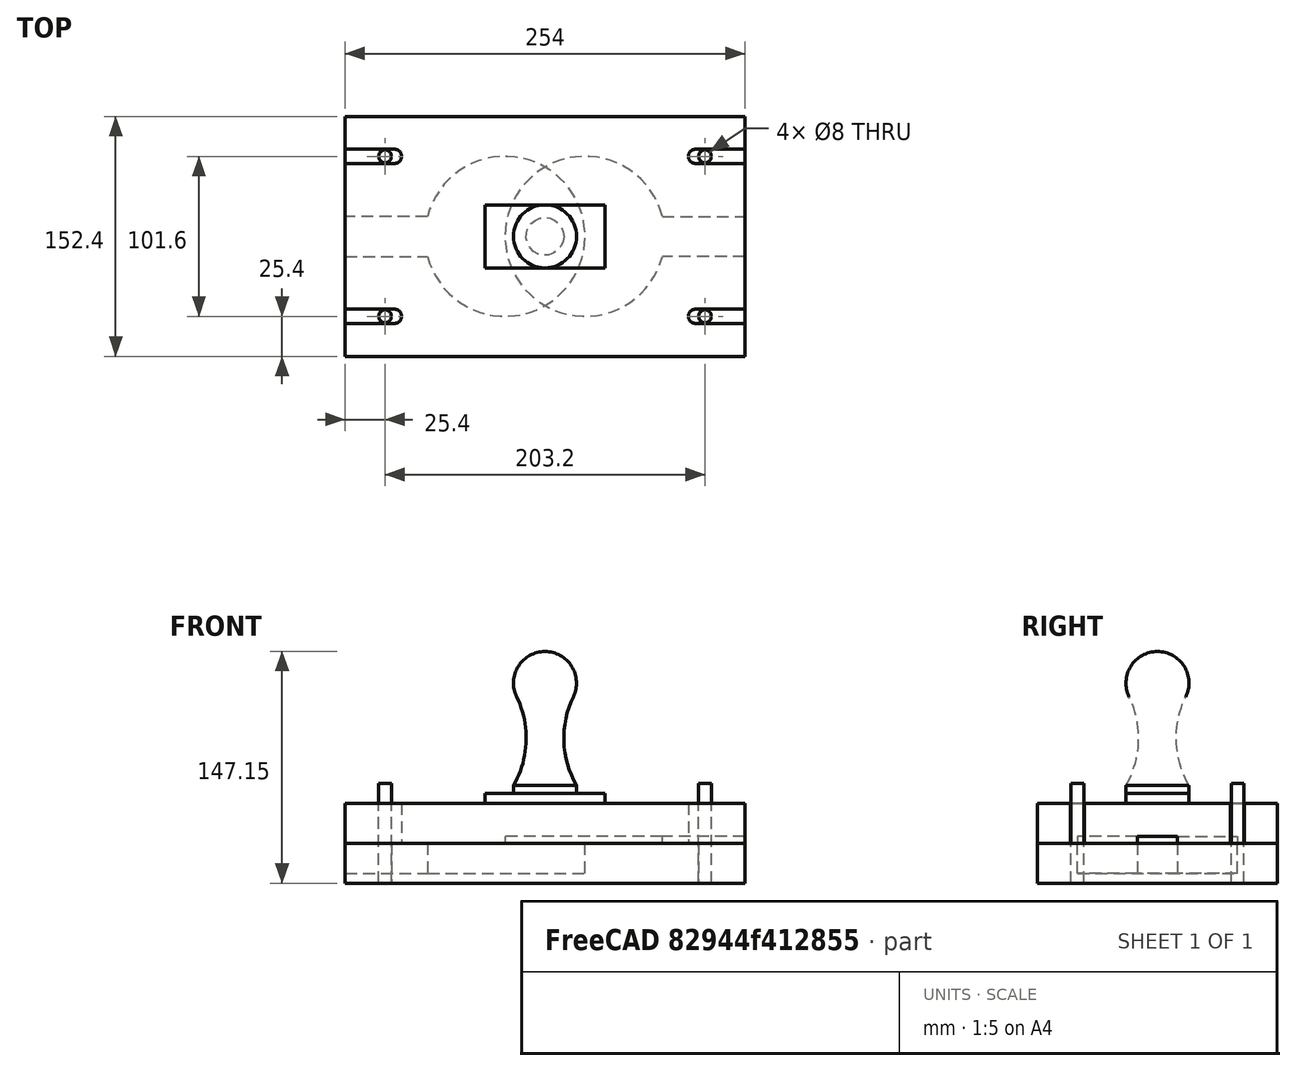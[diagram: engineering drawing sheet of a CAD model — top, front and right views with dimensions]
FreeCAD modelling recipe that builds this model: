
FCSTD DOCUMENT  (FreeCAD 0.17R13541 (Git))
Label: Bell-metal-detector-FEM
License: All rights reserved
LicenseURL: http://en.wikipedia.org/wiki/All_rights_reserved
objects: Sketcher::SketchObject×8, PartDesign::Pocket×4, Part::Cylinder×4, PartDesign::Mirrored×4, PartDesign::Pad×3, PartDesign::Body×3, Fem::FemSolverObjectPython×3, Fem::FemMeshObjectPython×3, PartDesign::MultiTransform×2, PartDesign::ShapeBinder×2, Part::Feature×2, Fem::ConstraintFixed×2, Fem::ConstraintForce×2, App::MaterialObjectPython×2, Fem::FemResultObjectPython×2, Fem::FemAnalysis×2, PartDesign::Revolution×1, Part::Compound×1, Part::Fuse×1, Fem::FemMeshShapeNetgenObject×1
note: 43 computed .brp shape members not serialized (recipe doc carries the construction recipe); baked Part::Feature solids carry a one-line shape summary decoded from their .brp

FEATURE [Sketcher::SketchObject] Sketch
  MapMode = 5
  Support = -> [XY_Plane]
  sketch-geometry (4):
    g0: LineSegment StartX=127 StartY=76.2 StartZ=0 EndX=-127 EndY=76.2 EndZ=0
    g1: LineSegment StartX=-127 StartY=76.2 StartZ=0 EndX=-127 EndY=-76.2 EndZ=0
    g2: LineSegment StartX=-127 StartY=-76.2 StartZ=0 EndX=127 EndY=-76.2 EndZ=0
    g3: LineSegment StartX=127 StartY=-76.2 StartZ=0 EndX=127 EndY=76.2 EndZ=0
  constraints (11):
    c: Coincident(g0,g1)
    c: Coincident(g1,g2)
    c: Coincident(g2,g3)
    c: Coincident(g3,g0)
    c: Horizontal(g0)
    c: Horizontal(g2)
    c: Vertical(g1)
    c: Vertical(g3)
    c: DistanceX(g0,g0) = 254
    c: DistanceY(g2,g0) = 152.4
    c: Symmetric(g0,g1,g-1)
FEATURE [PartDesign::Pad] Pad  label="上基座"
  Length = 25.4
  Length2 = 100
  Profile = -> Sketch
  Type = 0
FEATURE [Sketcher::SketchObject] Sketch001
  MapMode = 5
  Placement = pos=(0,0,25.4) rot=(0,0,1;0rad)
  Support = -> [Pad]
  sketch-geometry (1):
    g0: Circle CenterX=-101.6 CenterY=50.8 CenterZ=0 NormalX=0 NormalY=0 NormalZ=1 AngleXU=0 Radius=4
  constraints (3):
    c: DistanceX(g0) = -101.6
    c: DistanceY(g0) = 50.8
    c: Radius(g0) = 4
FEATURE [PartDesign::Pocket] Pocket  label="销钉孔"
  BaseFeature = -> Pad
  Length = 5
  Length2 = 100
  Profile = -> Sketch001
  Type = 1
FEATURE [Part::Cylinder] Cylinder  label="销钉1"
  Angle = 360
  AttacherType = Attacher::AttachEngine3D
  Height = 63.5
  Placement = pos=(-101.6,50.8,0) rot=(0,0,1;0rad)
  Radius = 4
FEATURE [Part::Cylinder] Cylinder001  label="销钉2"
  Angle = 360
  AttacherType = Attacher::AttachEngine3D
  Height = 63.5
  Placement = pos=(101.6,50.8,0) rot=(0,0,1;0rad)
  Radius = 4
FEATURE [Part::Cylinder] Cylinder002  label="销钉3"
  Angle = 360
  AttacherType = Attacher::AttachEngine3D
  Height = 63.5
  Placement = pos=(-101.6,-50.8,0) rot=(0,0,1;0rad)
  Radius = 4
FEATURE [Part::Cylinder] Cylinder003  label="销钉4"
  Angle = 360
  AttacherType = Attacher::AttachEngine3D
  Height = 63.5
  Placement = pos=(101.6,-50.8,0) rot=(0,0,1;0rad)
  Radius = 4
FEATURE [PartDesign::Mirrored] Mirrored
  MirrorPlane = -> YZ_Plane
FEATURE [PartDesign::Mirrored] Mirrored001
  MirrorPlane = -> XZ_Plane
FEATURE [PartDesign::MultiTransform] MultiTransform  label="两次镜像的销钉孔"
  BaseFeature = -> Pocket
  Originals = -> [Pocket]
  Transformations = -> [Mirrored,Mirrored001]
FEATURE [Sketcher::SketchObject] Sketch002
  ExternalGeometry = -> [MultiTransform]
  MapMode = 5
  Placement = pos=(0,0,25.4) rot=(0,0,1;0rad)
  Support = -> [MultiTransform]
  sketch-geometry (4):
    g0: LineSegment StartX=-127 StartY=-12.7 StartZ=0 EndX=-74.5869 EndY=-12.7 EndZ=0
    g1: LineSegment StartX=-74.5869 StartY=12.7 StartZ=0 EndX=-127 EndY=12.7 EndZ=0
    g2: LineSegment StartX=-127 StartY=12.7 StartZ=0 EndX=-127 EndY=-12.7 EndZ=0
    g3: ArcOfCircle CenterX=-25.4 CenterY=0 CenterZ=0 NormalX=0 NormalY=0 NormalZ=1 AngleXU=0 Radius=50.8 StartAngle=3.39427 EndAngle=9.1721
  constraints (13):
    c: Coincident(g1,g2)
    c: Coincident(g2,g0)
    c: Horizontal(g0)
    c: Horizontal(g1)
    c: Vertical(g2)
    c: PointOnObject(g0,g-3)
    c: PointOnObject(g3,g-1)  '凹坑中心在x轴上'
    c: Symmetric(g1,g0,g-1)  '沟槽中心对称'
    c: DistanceY(g0,g1) = 25.4  '沟槽宽度'
    c: Radius(g3) = 50.8  '凹坑半径'
    c: DistanceX(g3,g-1) = 25.4  '凹坑位置'
    c: Coincident(g3,g0)
    c: Coincident(g3,g1)
FEATURE [PartDesign::Pocket] Pocket001  label="深沟槽和凹坑"
  BaseFeature = -> MultiTransform
  Length = 19.05
  Length2 = 100
  Profile = -> Sketch002
  Type = 0
FEATURE [PartDesign::Body] Body  label="下底座"
  Group = -> [Sketch,Pad,Sketch001,Pocket,MultiTransform,Mirrored,Mirrored001,Sketch002,Pocket001]
  Origin = -> Origin
  Tip = -> Pocket001
FEATURE [PartDesign::ShapeBinder] ShapeBinder  label="引用的下底座的顶面"
  Support = -> [Pocket001]
FEATURE [Sketcher::SketchObject] Sketch003
  ExternalGeometry = -> [ShapeBinder]
  MapMode = 5
  Placement = pos=(0,0,25.4) rot=(0,0,1;0rad)
  Support = -> [ShapeBinder]
  sketch-geometry (4):
    g0: LineSegment StartX=-127 StartY=76.2 StartZ=0 EndX=127 EndY=76.2 EndZ=0
    g1: LineSegment StartX=127 StartY=76.2 StartZ=0 EndX=127 EndY=-76.2 EndZ=0
    g2: LineSegment StartX=127 StartY=-76.2 StartZ=0 EndX=-127 EndY=-76.2 EndZ=0
    g3: LineSegment StartX=-127 StartY=-76.2 StartZ=0 EndX=-127 EndY=76.2 EndZ=0
  constraints (10):
    c: Coincident(g0,g1)
    c: Coincident(g1,g2)
    c: Coincident(g2,g3)
    c: Coincident(g3,g0)
    c: Horizontal(g0)
    c: Horizontal(g2)
    c: Vertical(g1)
    c: Vertical(g3)
    c: Coincident(g0,g-3)
    c: Coincident(g1,g-4)
FEATURE [PartDesign::Pad] Pad001  label="下基座"
  Length = 25.4
  Length2 = 100
  Profile = -> Sketch003
  Type = 0
FEATURE [Sketcher::SketchObject] Sketch004
  ExternalGeometry = -> [ShapeBinder]
  MapMode = 5
  Placement = pos=(0,0,25.4) rot=(0,0,1;0rad)
  Support = -> [ShapeBinder]
  sketch-geometry (5):
    g0: LineSegment [constr] StartX=-101.6 StartY=50.8 StartZ=0 EndX=-95.6 EndY=50.8 EndZ=0
    g1: ArcOfCircle CenterX=-95.6 CenterY=50.8 CenterZ=0 NormalX=0 NormalY=0 NormalZ=1 AngleXU=0 Radius=4.5 StartAngle=4.71239 EndAngle=7.85398
    g2: LineSegment StartX=-95.6 StartY=55.3 StartZ=0 EndX=-127 EndY=55.3 EndZ=0
    g3: LineSegment StartX=-127 StartY=55.3 StartZ=0 EndX=-127 EndY=46.3 EndZ=0
    g4: LineSegment StartX=-127 StartY=46.3 StartZ=0 EndX=-95.6 EndY=46.3 EndZ=0
  constraints (13):
    c: Coincident(g0,g-3)
    c: Horizontal(g0)
    c: Coincident(g1,g0)
    c: PointOnObject(g2,g-4)
    c: Horizontal(g2)
    c: Coincident(g3,g2)
    c: Coincident(g4,g3)
    c: Horizontal(g4)
    c: Tangent(g4,g1) = -1.5708
    c: Tangent(g2,g1) = -1.5708
    c: DistanceX(g0,g0) = 6
    c: Radius(g1) = 4.5
    c: Vertical(g3)
FEATURE [PartDesign::Pocket] Pocket002  label="滑槽"
  BaseFeature = -> Pad001
  Length = 5
  Length2 = 100
  Profile = -> Sketch004
  Reversed = true
  Type = 1
FEATURE [Sketcher::SketchObject] Sketch005
  ExternalGeometry = -> [ShapeBinder]
  MapMode = 5
  Placement = pos=(0,0,25.4) rot=(0,0,1;0rad)
  Support = -> [ShapeBinder]
  sketch-geometry (5):
    g0: LineSegment [constr] StartX=-74.5869 StartY=12.7 StartZ=0 EndX=-74.5869 EndY=-12.7 EndZ=0
    g1: LineSegment StartX=127 StartY=-12.7 StartZ=0 EndX=74.5869 EndY=-12.7 EndZ=0
    g2: LineSegment StartX=74.5869 StartY=12.7 StartZ=0 EndX=127 EndY=12.7 EndZ=0
    g3: LineSegment StartX=127 StartY=12.7 StartZ=0 EndX=127 EndY=-12.7 EndZ=0
    g4: ArcOfCircle CenterX=25.4 CenterY=0 CenterZ=0 NormalX=0 NormalY=0 NormalZ=1 AngleXU=0 Radius=50.8 StartAngle=0.25268 EndAngle=6.03051
  constraints (15):
    c: Coincident(g0,g-3)
    c: Coincident(g0,g-3)
    c: Coincident(g2,g3)
    c: Coincident(g3,g1)
    c: Horizontal(g1)
    c: Horizontal(g2)
    c: Vertical(g3)
    c: PointOnObject(g1,g-4)
    c: PointOnObject(g4,g-1)
    c: Symmetric(g2,g1,g-1)  '沟槽沿x轴对称'
    c: Equal(g3,g0)  '沟槽宽度相等'
    c: Equal(g4,g-3)  '两圆大小相等'
    c: Coincident(g4,g2)
    c: Coincident(g4,g1)
    c: Symmetric(g4,g-3,g-1)  '两圆镜像'
FEATURE [PartDesign::Pocket] Pocket003  label="浅沟槽和凹坑"
  BaseFeature = -> Pocket002
  Length = 4.318
  Length2 = 100
  Profile = -> Sketch005
  Reversed = true
  Type = 0
FEATURE [PartDesign::Mirrored] Mirrored002
  MirrorPlane = -> YZ_Plane001
FEATURE [PartDesign::Mirrored] Mirrored003
  MirrorPlane = -> XZ_Plane001
FEATURE [PartDesign::MultiTransform] MultiTransform001  label="两次镜像的滑槽"
  BaseFeature = -> Pocket003
  Originals = -> [Pocket002]
  Transformations = -> [Mirrored002,Mirrored003]
FEATURE [PartDesign::Body] Body001  label="上部块"
  Group = -> [ShapeBinder,Sketch003,Pad001,Sketch004,Pocket002,Sketch005,Pocket003,MultiTransform001,Mirrored002,Mirrored003]
  Origin = -> Origin001
  Tip = -> MultiTransform001
FEATURE [PartDesign::ShapeBinder] ShapeBinder001  label="引用的上部块的顶面"
  Support = -> [MultiTransform001]
FEATURE [Sketcher::SketchObject] Sketch006
  MapMode = 5
  Placement = pos=(0,0,50.8) rot=(0,0,1;0rad)
  Support = -> [ShapeBinder001]
  sketch-geometry (4):
    g0: LineSegment StartX=38.1 StartY=20 StartZ=0 EndX=-38.1 EndY=20 EndZ=0
    g1: LineSegment StartX=-38.1 StartY=20 StartZ=0 EndX=-38.1 EndY=-20 EndZ=0
    g2: LineSegment StartX=-38.1 StartY=-20 StartZ=0 EndX=38.1 EndY=-20 EndZ=0
    g3: LineSegment StartX=38.1 StartY=-20 StartZ=0 EndX=38.1 EndY=20 EndZ=0
  constraints (11):
    c: Coincident(g0,g1)
    c: Coincident(g1,g2)
    c: Coincident(g2,g3)
    c: Coincident(g3,g0)
    c: Horizontal(g0)
    c: Horizontal(g2)
    c: Vertical(g1)
    c: Vertical(g3)
    c: Symmetric(g0,g1,g-1)
    c: DistanceX(g0,g0) = 76.2
    c: DistanceY(g2,g0) = 40
FEATURE [PartDesign::Pad] Pad002  label="手柄座"
  Length = 6.35
  Length2 = 100
  Profile = -> Sketch006
  Type = 0
FEATURE [Sketcher::SketchObject] Sketch007
  ExternalGeometry = -> [Pad002]
  MapMode = 5
  Placement = pos=(0,0,0) rot=(1,0,0;1.5708rad)
  Support = -> [XZ_Plane002]
  sketch-geometry (5):
    g0: LineSegment StartX=0 StartY=57.15 StartZ=0 EndX=20 EndY=57.15 EndZ=0
    g1: LineSegment StartX=20 StartY=57.15 StartZ=0 EndX=20 EndY=62.15 EndZ=0
    g2: ArcOfCircle CenterX=71.9485 CenterY=92.1726 CenterZ=0 NormalX=0 NormalY=0 NormalZ=1 AngleXU=0 Radius=60 StartAngle=2.68909 EndAngle=3.66563
    g3: ArcOfCircle CenterX=0 CenterY=127.15 CenterZ=0 NormalX=0 NormalY=0 NormalZ=1 AngleXU=0 Radius=20 StartAngle=5.83068 EndAngle=7.85398
    g4: LineSegment StartX=0 StartY=147.15 StartZ=0 EndX=0 EndY=57.15 EndZ=0
  constraints (16):
    c: PointOnObject(g0,g-3)
    c: PointOnObject(g0,g-3)
    c: Coincident(g0,g1)
    c: Vertical(g1)
    c: Coincident(g2,g1)
    c: Coincident(g4,g3)
    c: Coincident(g4,g0)
    c: Vertical(g4)
    c: Perpendicular(g3,g4)
    c: PointOnObject(g4,g-2)
    c: Tangent(g3,g2) = 1.5708
    c: DistanceX(g0,g0) = 20
    c: DistanceY(g0,g1) = 5
    c: Radius(g2) = 60
    c: DistanceY(g0,g3) = 90
    c: DistanceY(g0,g3) = 70
FEATURE [PartDesign::Revolution] Revolution  label="把手"
  Angle = 360
  Axis = (0,0,1)
  Base = (0,0,0)
  BaseFeature = -> Pad002
  Profile = -> Sketch007
  ReferenceAxis = -> Sketch007 [V_Axis]
  Reversed = true
FEATURE [PartDesign::Body] Body002  label="手柄"
  Group = -> [ShapeBinder001,Sketch006,Pad002,Sketch007,Revolution]
  Origin = -> Origin002
  Tip = -> Revolution
FEATURE [Part::Compound] Compound  label="四个销钉"
  Links = -> [Cylinder,Cylinder001,Cylinder003,Cylinder002]
FEATURE [Fem::FemSolverObjectPython] CalculiXccxTools  # FEM object (typed FeaturePython)
  AnalysisType = 0
  BeamShellResultOutput3D = false
  EigenmodeHighLimit = 1000000
  EigenmodeLowLimit = 0
  EigenmodesCount = 10
  GeometricalNonlinearity = 0
  IterationsControlParameterCutb = 0.25,0.5,0.75,0.85,,,1.5,
  IterationsControlParameterIter = 4,8,9,200,10,400,,200,,
  IterationsControlParameterTimeUse = false
  IterationsThermoMechMaximum = 2000
  IterationsUserDefinedIncrementations = false
  IterationsUserDefinedTimeStepLength = false
  MaterialNonlinearity = 0
  MatrixSolverType = 0
  SplitInputWriter = false
  ThermoMechSteadyState = true
  TimeEnd = 1
  TimeInitialStep = 0.01
FEATURE [Part::Feature] Body001001  label="upper body"
  shape: bbox 254 x 152.4 x 25.4 mm, 26 faces (baked)
FEATURE [Part::Feature] Body002001  label="handle"
  shape: bbox 76.2 x 63.53 x 97.58 mm, 10 faces (baked)
FEATURE [Part::Fuse] Fusion  label="fusion-for-fem"
  Base = -> Body001001
  Tool = -> Body002001
FEATURE [Fem::FemSolverObjectPython] CalculiXccxTools001  # FEM object (typed FeaturePython)
  AnalysisType = 0
  BeamShellResultOutput3D = false
  EigenmodeHighLimit = 1000000
  EigenmodeLowLimit = 0
  EigenmodesCount = 10
  GeometricalNonlinearity = 0
  IterationsControlParameterCutb = 0.25,0.5,0.75,0.85,,,1.5,
  IterationsControlParameterIter = 4,8,9,200,10,400,,200,,
  IterationsControlParameterTimeUse = false
  IterationsThermoMechMaximum = 2000
  IterationsUserDefinedIncrementations = false
  IterationsUserDefinedTimeStepLength = false
  MaterialNonlinearity = 0
  MatrixSolverType = 0
  SplitInputWriter = false
  ThermoMechSteadyState = true
  TimeEnd = 1
  TimeInitialStep = 0.01
FEATURE [Fem::FemMeshObjectPython] FEMMeshGmsh001  # FEM object (typed FeaturePython)
  Algorithm2D = 0
  Algorithm3D = 0
  CharacteristicLengthMax = 0
  CharacteristicLengthMin = 0
  CoherenceMesh = true
  ElementDimension = 0
  ElementOrder = 1
  GeometryTolerance = 1e-06
  GroupsOfNodes = false
  HighOrderOptimize = false
  OptimizeNetgen = false
  OptimizeStd = true
  Part = -> Fusion
  RecombineAll = false
FEATURE [Fem::ConstraintFixed] FemConstraintFixed001
  NormalDirection = (0,0,-1)
  Normals = (14) [(0,0,-1),(0,0,-1),(0,0,-1),(0,0,-1),(0,0,-1),(0,0,-1),(0,0,-1),(0,0,-1),(0,0,-1),(0,0,-1),(0,0,-1),(0,0,-1),(0,0,-1),(0,0,-1)]
  Points = (14) [(127,-76.2,25.4),(42.3333,-76.2,25.4),(-42.3333,-76.2,25.4),(-127,-76.2,25.4),(127,-25.4,25.4),(-42.3333,-25.4,25.4),(-127,-25.4,25.4),+7 more]
  References = -> [Fusion]
  Scale = 15
FEATURE [Fem::ConstraintForce] FemConstraintForce001
  DirectionVector = (1,0,0)
  Force = 9000
  NormalDirection = (-1,0,0)
  Points = (56) [(-38.1,20,57.15),(-38.1,6.66667,57.15),(-38.1,-6.66667,57.15),(-38.1,-20,57.15),(-38.1,20,53.975),(-38.1,6.66667,53.975),(-38.1,-6.66667,53.975),+49 more]
  References = -> [Fusion]
  Reversed = true
  Scale = 6
FEATURE [App::MaterialObjectPython] SolidMaterial001  # material (typed FeaturePython)
  Category = 0
  Material = Density=700.0 kg/m^3,Description=A standard construction wood,Father=Aggregate,Name=Wood,PoissonRatio=0.05,+5 more (map truncated)
FEATURE [Fem::FemMeshObjectPython] Result_mesh  # FEM object (typed FeaturePython)
FEATURE [Fem::FemResultObjectPython] CalculiX_static_results  # FEM object (typed FeaturePython)
  DisplacementLengths = [0,9.68372e-05,0,0.00024978,0,6.92181e-05,0,0.000142214,0,0,0,0,0,0,0,0,0,0,0,0,0,0,0,0,0,0,0,0,0.00013679,0.00020387,0.000155959,0.000156177,0.000202629,0.000135248,0.000559087,6.85422e-05,0.00114178,9.57881e-05,0.000389853,0.000245105,+2379 more]
  DisplacementVectors = (2419) [(0,0,0),(8.24847e-05,-2.54458e-05,4.38889e-05),(0,0,0),(-0.000172944,-0.000130977,0.000123796),(0,0,0),(6.23805e-05,-2.56127e-05,1.56143e-05),(0,0,0),+2412 more]
  Eigenmode = 0
  EigenmodeFrequency = 0
  MaxShear = [0.0313368,0.00386722,0.0886737,0.013198,0.0136742,0.00920001,0.0228507,0.0372929,0.0482589,0.0483114,0.0920672,0.059342,0.0136504,0.0310515,0.0871576,0.0229919,0.144081,0.171755,0.128968,0.183178,7.43563,6.91888,0.186055,0.133686,0.177813,+2394 more]
  Mesh = -> Result_mesh
  NodeNumbers = [1,2,3,4,5,6,7,8,9,10,11,12,13,14,15,16,17,18,19,20,21,22,23,24,25,26,27,28,29,30,31,32,33,34,35,36,37,38,39,40,41,42,43,44,45,46,47,48,49,50,51,52,53,54,55,56,57,58,59,60,61,62,63,64,65,66,67,68,69,+2350 more]
  PrincipalMax = [0.0565926,0.00155221,0.157903,0.00537805,0.0224719,0.00492786,0.0057609,0.0169741,0.0879244,0.0878953,0.120696,0.0704882,0.0224386,0.0560357,0.155151,0.00544304,0.162887,0.300473,0.23437,0.38353,3.3663,3.30481,0.389924,0.241005,0.32923,+2394 more]
  PrincipalMed = [0.00108195,-0.003982,0.00343419,-0.00558212,-0.000626649,-0.00737385,-0.00191118,-0.0269215,0.00281702,0.00276914,0.00571473,0.00462064,-0.00060989,0.0010661,0.00343031,-0.00192474,0.00664831,0.0137384,-0.00173009,0.0266679,-0.451423,+2398 more]
  PrincipalMin = [-0.00608101,-0.00618222,-0.0194447,-0.0210179,-0.00487651,-0.0134722,-0.0399404,-0.0576117,-0.00859345,-0.00872745,-0.0634387,-0.0481957,-0.00486214,-0.00606729,-0.0191647,-0.0405407,-0.125276,-0.0430376,-0.0235651,0.0171745,-11.505,+2398 more]
  ResultType = Fem::FemResultMechanical
  Stats = [-0.0142135,0.0681837,2.21858,-0.0121677,-8.08586e-05,0.0127033,-0.665219,-0.00543383,0.609878,0,0.0744099,2.21875,0.00109784,3.55157,112.634,-5.4292,1.77361,105.491,-28.499,-0.158746,28.0703,-113.467,-2.15065,1.20046,0.000630505,1.96213,+13 more]
  StrainVectors = (2419) [(-1.63201e-07,-9.05111e-08,4.12322e-06),(-3.32673e-07,-2.49892e-08,-2.88238e-07),(-3.25155e-07,-3.91413e-07,1.13585e-05),+2416 more]
  StressValues = [0.0594168,0.00690253,0.167087,0.0229688,0.0254906,0.0162339,0.0423893,0.0649298,0.0913486,0.0914182,0.161103,0.10299,0.0254426,0.0588614,0.164188,0.0427784,0.249852,0.318935,0.247741,0.361702,13.3774,12.4428,0.367781,0.255737,0.346977,+2394 more]
  StressVectors = (2419) [(0.00059168,0.00142242,0.0495794),(-0.00421207,-0.000695686,-0.00370425),(0.0030407,0.00228346,0.136568),(-0.00745803,-0.000709604,-0.0130543),+2415 more]
  Time = 0
  UserDefined = [0.0626736,0.00773443,0.177347,0.0263959,0.0273484,0.0184,0.0457013,0.0745858,0.0965178,0.0966228,0.184134,0.118684,0.0273008,0.062103,0.174315,0.0459838,0.288162,0.34351,0.257935,0.366355,14.8713,13.8378,0.37211,0.267372,0.355625,0.292015,+2393 more]
FEATURE [Fem::FemAnalysis] Analysis001
  Group = -> [CalculiXccxTools001,FEMMeshGmsh001,FemConstraintFixed001,FemConstraintForce001,SolidMaterial001,CalculiX_static_results]
FEATURE [Fem::FemSolverObjectPython] CalculiXccxTools002  # FEM object (typed FeaturePython)
  AnalysisType = 0
  BeamShellResultOutput3D = false
  EigenmodeHighLimit = 1000000
  EigenmodeLowLimit = 0
  EigenmodesCount = 10
  GeometricalNonlinearity = 0
  IterationsControlParameterCutb = 0.25,0.5,0.75,0.85,,,1.5,
  IterationsControlParameterIter = 4,8,9,200,10,400,,200,,
  IterationsControlParameterTimeUse = false
  IterationsThermoMechMaximum = 2000
  IterationsUserDefinedIncrementations = false
  IterationsUserDefinedTimeStepLength = false
  MaterialNonlinearity = 0
  MatrixSolverType = 0
  SplitInputWriter = false
  ThermoMechSteadyState = true
  TimeEnd = 1
  TimeInitialStep = 0.01
FEATURE [Fem::FemMeshShapeNetgenObject] FEMMeshNetgen
  Fineness = 2
  GrowthRate = 0.3
  MaxSize = 1000
  NbSegsPerEdge = 1
  NbSegsPerRadius = 2
  Optimize = true
  SecondOrder = true
  Shape = -> Fusion
FEATURE [Fem::ConstraintFixed] FemConstraintFixed
  NormalDirection = (0,0,-1)
  Normals = (14) [(0,0,-1),(0,0,-1),(0,0,-1),(0,0,-1),(0,0,-1),(0,0,-1),(0,0,-1),(0,0,-1),(0,0,-1),(0,0,-1),(0,0,-1),(0,0,-1),(0,0,-1),(0,0,-1)]
  Points = (14) [(127,-76.2,25.4),(42.3333,-76.2,25.4),(-42.3333,-76.2,25.4),(-127,-76.2,25.4),(127,-25.4,25.4),(-42.3333,-25.4,25.4),(-127,-25.4,25.4),+7 more]
  References = -> [Fusion]
  Scale = 15
FEATURE [Fem::ConstraintForce] FemConstraintForce
  DirectionVector = (1,0,0)
  Force = 9000
  NormalDirection = (-1,0,0)
  Points = (44) [(20,1.269e-14,57.15),(-10,-17.3205,57.15),(-10,17.3205,57.15),(20,1.75886e-14,57.15),(20,1.324e-14,59.65),(-10,-17.3205,59.65),(-10,17.3205,59.65),+37 more]
  References = -> [Fusion]
  Reversed = true
  Scale = 6
FEATURE [App::MaterialObjectPython] SolidMaterial  # material (typed FeaturePython)
  Category = 0
  Material = Density=700.0 kg/m^3,Description=A standard construction wood,Father=Aggregate,Name=Wood,PoissonRatio=0.05,+5 more (map truncated)
FEATURE [Fem::FemMeshObjectPython] Result_mesh001  # FEM object (typed FeaturePython)
FEATURE [Fem::FemResultObjectPython] CalculiX_static_results001  # FEM object (typed FeaturePython)
  DisplacementLengths = [2.64989,1.69263,0.158017,0.114155,0.0551497,0.0597413,0.0103731,0.0592073,0.0551254,0.0104688,0.0078468,0.00786399,0.000205543,0.000207401,0.054398,0.00649878,0.0544517,0.00660444,0.000679879,0.00119933,0.00016513,0.000517936,0.000307307,+31637 more]
  DisplacementVectors = (31660) [(2.64972,-3.14191e-05,-0.029672),(1.53096,-0.000181975,-0.72192),(0.0724646,-7.73756e-05,-0.140422),(0.0277466,9.55491e-06,-0.110732),+31656 more]
  Eigenmode = 0
  EigenmodeFrequency = 0
  MaxShear = [0.843332,3.75503,19.0607,41.0073,0.871618,3.97184,2.15419,2.53293,1.01103,1.18867,9.03798,9.90125,0.287496,0.301927,6.68736,3.74111,7.8169,3.7922,0.200354,0.139941,0.00218836,0.00861129,0.00784671,0.00999896,0.00316805,0.150166,0.000957025,+31633 more]
  Mesh = -> Result_mesh001
  NodeNumbers = [1,2,3,4,5,6,7,8,9,10,11,12,13,14,15,16,17,18,19,20,21,22,23,24,25,26,27,28,29,30,31,32,33,34,35,36,37,38,39,40,41,42,43,44,45,46,47,48,49,50,51,52,53,54,55,56,57,58,59,60,61,62,63,64,65,66,67,68,69,+31591 more]
  PrincipalMax = [0.885911,1.27254,0.456945,-1.18514,0.599398,6.59369,0.695077,3.82291,0.687875,0.530314,1.35334,1.26049,0.538385,0.563637,-2.95847,6.36452,-2.38862,6.42167,0.388991,0.263809,0.00122269,0.00659138,0.00363194,0.00610974,0.00228961,0.285396,+31634 more]
  PrincipalMed = [-0.0486711,-1.11456,-2.07196,-39.9453,-0.167665,3.3157,-1.24504,2.23994,-0.114809,-0.933142,-5.88561,-7.17867,0.0927254,0.0848733,-6.82257,2.48925,-7.17521,2.88176,0.0277059,0.018127,-0.000549243,-0.00629464,-0.000892908,-0.00684803,+31636 more]
  PrincipalMin = [-0.800752,-6.23753,-37.6645,-83.1998,-1.14384,-1.34998,-3.6133,-1.24295,-1.33419,-1.84703,-16.7226,-18.542,-0.0366059,-0.0402162,-16.3332,-1.11771,-18.0224,-1.16273,-0.0117174,-0.0160733,-0.00315402,-0.0106312,-0.0120615,-0.0138882,+31636 more]
  ResultType = Fem::FemResultMechanical
  Stats = [-0.0190824,0.0385734,2.64972,-0.0159492,8.83308e-05,0.0158355,-0.802965,-0.0114644,0.74344,0,0.047456,2.64989,0.000922238,6.62637,148.987,-7.79408,3.16238,152.547,-50.2183,-0.36559,44.9424,-149.73,-4.11797,3.30321,0.000529374,3.64017,+13 more]
  StrainVectors = (31660) [(-4.36731e-06,-3.03136e-06,1.01353e-05),(0.000136238,-9.92159e-05,-0.000492988),(-1.49508e-05,-4.21007e-05,-0.00288891),+31657 more]
  StressValues = [1.46354,6.64621,36.922,71.0623,1.5133,6.91433,3.7373,4.48883,1.76351,2.0771,15.7573,17.2117,0.522472,0.552042,11.922,6.48119,13.8742,6.57313,0.382524,0.264446,0.00381315,0.0155157,0.013991,0.0175696,0.0059705,0.286874,0.00170531,0.42874,+31632 more]
  StressVectors = (31660) [(-0.0481746,-0.0329065,0.117569),(1.2675,-1.4234,-5.92365),(-2.04132,-2.3516,-34.8866),(-39.9596,-14.5184,-69.8523),(0.0933749,-0.00649416,-0.798986),+31655 more]
  Time = 0
  UserDefined = [1.68666,7.51006,38.1215,82.0147,1.74324,7.94368,4.30838,5.06586,2.02207,2.37735,18.076,19.8025,0.574991,0.603853,13.3747,7.48223,15.6338,7.5844,0.400709,0.279882,0.00437672,0.0172226,0.0156934,0.0199979,0.00633611,0.300331,0.00191405,+31633 more]
FEATURE [Fem::FemAnalysis] Analysis
  Group = -> [CalculiXccxTools002,FEMMeshNetgen,FemConstraintFixed,FemConstraintForce,SolidMaterial,CalculiX_static_results001]
